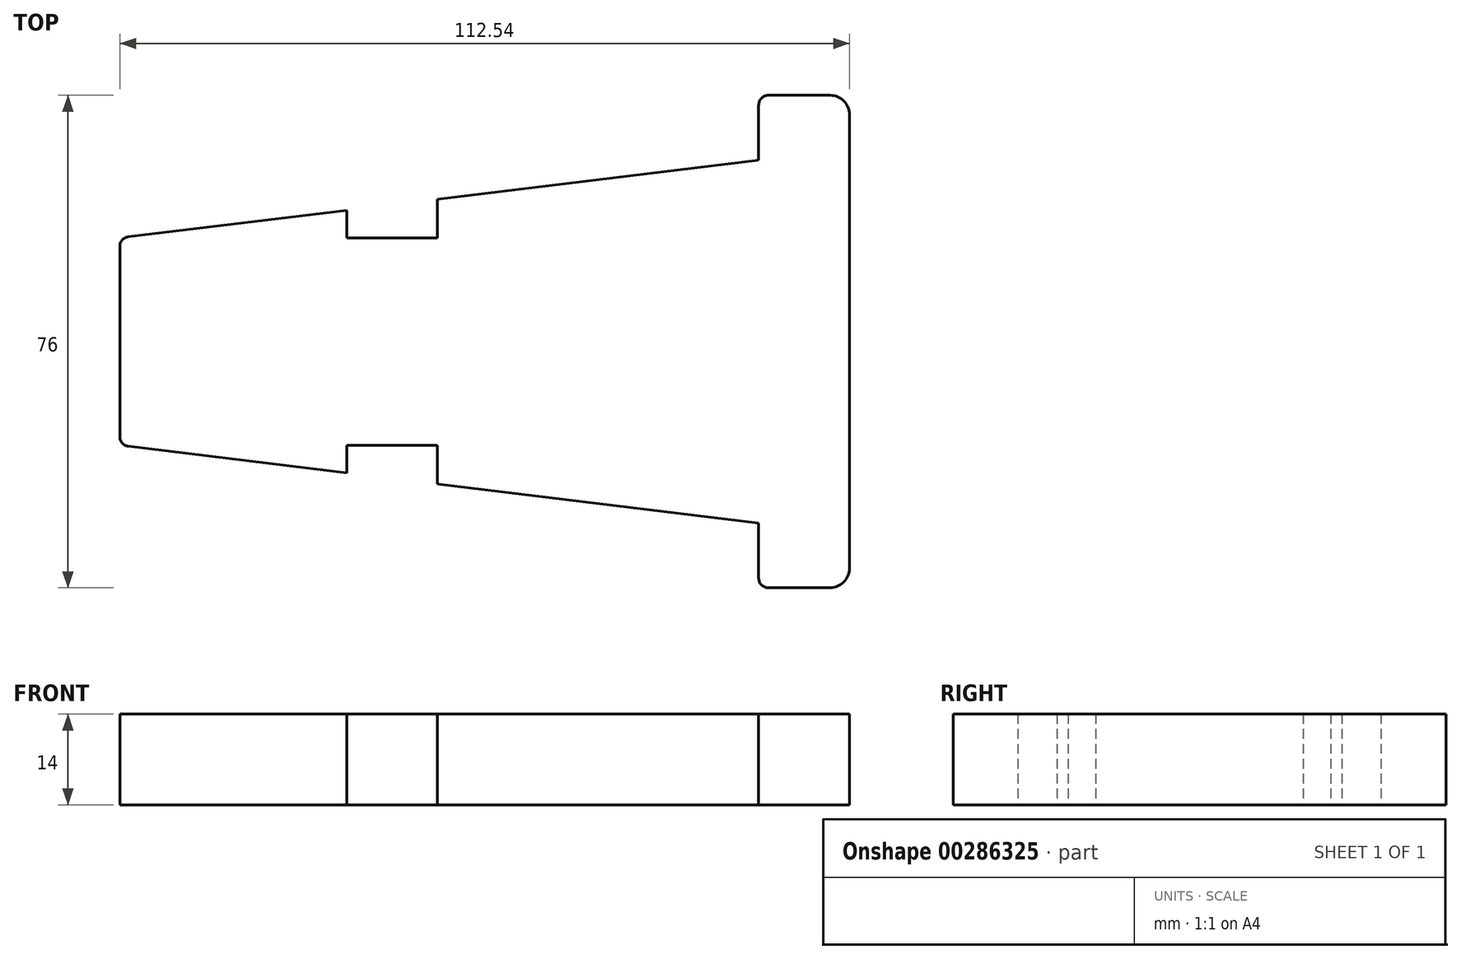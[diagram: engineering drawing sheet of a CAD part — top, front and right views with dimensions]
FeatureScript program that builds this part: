
annotation { "Feature Type Name" : "Feature", "Feature Type Description" : "" }
export const myFeature = defineFeature(function(context is Context, id is Id, definition is map)
    precondition{}
    {
        {
            var Q0;
            Q0=qCreatedBy(makeId("Top.planeOp"),FACE);
            var sketch = newSketch(context, id + "F0", { "sketchPlane" : qUnion([Q0])});
            skLineSegment(sketch, "E0", {"start": v(56.71, 35) * mm, "end": v(56.71, -35) * mm});
            skLineSegment(sketch, "E1", {"start": v(53.71, 38) * mm, "end": v(44.21, 38) * mm});
            skLineSegment(sketch, "E2", {"start": v(53.71, -38) * mm, "end": v(44.21, -38) * mm});
            skLineSegment(sketch, "E3", {"start": v(42.71, 36.5) * mm, "end": v(42.71, 28) * mm});
            skLineSegment(sketch, "E4", {"start": v(42.71, -36.5) * mm, "end": v(42.71, -28) * mm});
            skPoint(sketch, "E5.orphan", {"position": v(21.88, 18) * mm});
            skPoint(sketch, "E6.orphan", {"position": v(21.88, -18) * mm});
            skPoint(sketch, "E7.visualSharp", {"position": v(56.71, 38) * mm});
            skArc(sketch, "E7.filletArc", {"start": v(56.71, 35) * mm, "mid": v(55.83, 37.12) * mm, "end": v(53.71, 38) * mm});
            skPoint(sketch, "E8.visualSharp", {"position": v(56.71, -38) * mm});
            skArc(sketch, "E8.filletArc", {"start": v(53.71, -38) * mm, "mid": v(55.83, -37.12) * mm, "end": v(56.71, -35) * mm});
            skPoint(sketch, "E9.visualSharp", {"position": v(-41.66, 14) * mm});
            skPoint(sketch, "E10.visualSharp", {"position": v(-48.29, -18) * mm});
            skPoint(sketch, "E11.visualSharp", {"position": v(42.71, 38) * mm});
            skArc(sketch, "E11.filletArc", {"start": v(44.21, 38) * mm, "mid": v(43.15, 37.56) * mm, "end": v(42.71, 36.5) * mm});
            skPoint(sketch, "E12.start.orphan", {"position": v(6.97, 15.5) * mm});
            skPoint(sketch, "E13.start.orphan", {"position": v(6.97, -18) * mm});
            skPoint(sketch, "E14.start.orphan", {"position": v(-6.83, -18) * mm});
            skLineSegment(sketch, "E15", {"start": v(6.97, 15.5) * mm, "end": v(6.97, 14) * mm});
            skLineSegment(sketch, "E16.trimOffspring", {"start": v(-6.86, 14) * mm, "end": v(-6.83, 14) * mm});
            skLineSegment(sketch, "E17", {"start": v(6.97, -18) * mm, "end": v(6.97, -17.77) * mm});
            skLineSegment(sketch, "E18.trimOffspring", {"start": v(-6.85, -17.83) * mm, "end": v(-6.83, -17.83) * mm});
            skPoint(sketch, "E19.visualSharp", {"position": v(42.71, -38) * mm});
            skArc(sketch, "E19.filletArc", {"start": v(42.71, -36.5) * mm, "mid": v(43.15, -37.56) * mm, "end": v(44.21, -38) * mm});
            skLineSegment(sketch, "E20", {"start": v(-6.83, -17.83) * mm, "end": v(-6.83, -18) * mm});
            skLineSegment(sketch, "E21", {"start": v(-55.83, 0) * mm, "end": v(-55.83, -16) * mm});
            skLineSegment(sketch, "E22", {"start": v(-55.83, -14.67) * mm, "end": v(-55.83, 0) * mm});
            skLineSegment(sketch, "E23", {"start": v(-55.83, 14.67) * mm, "end": v(-55.83, 0) * mm});
            skLineSegment(sketch, "E24", {"start": v(-54.52, -16.16) * mm, "end": v(-20.83, -20.26) * mm});
            skLineSegment(sketch, "E25", {"start": v(-54.52, 16.16) * mm, "end": v(-20.83, 20.26) * mm});
            skLineSegment(sketch, "E26", {"start": v(-20.83, 16) * mm, "end": v(-6.83, 16) * mm});
            skLineSegment(sketch, "E27", {"start": v(-20.83, -16) * mm, "end": v(-6.83, -16) * mm});
            skLineSegment(sketch, "E28", {"start": v(-6.83, -16) * mm, "end": v(-6.83, -21.97) * mm});
            skLineSegment(sketch, "E29", {"start": v(-6.83, 16) * mm, "end": v(-6.83, 21.97) * mm});
            skLineSegment(sketch, "E30", {"start": v(-20.83, -20.26) * mm, "end": v(-20.83, -16) * mm});
            skLineSegment(sketch, "E31", {"start": v(-20.83, 16) * mm, "end": v(-20.83, 20.26) * mm});
            skLineSegment(sketch, "E32.trimOffspring", {"start": v(-6.83, 21.97) * mm, "end": v(42.71, 28) * mm});
            skLineSegment(sketch, "E33.trimOffspring", {"start": v(-6.83, -21.97) * mm, "end": v(42.71, -28) * mm});
            skPoint(sketch, "E34.visualSharp", {"position": v(-55.83, 16) * mm});
            skArc(sketch, "E34.filletArc", {"start": v(-54.52, 16.16) * mm, "mid": v(-55.46, 15.67) * mm, "end": v(-55.83, 14.67) * mm});
            skPoint(sketch, "E35.visualSharp", {"position": v(-55.83, -16) * mm});
            skArc(sketch, "E35.filletArc", {"start": v(-55.83, -14.67) * mm, "mid": v(-55.46, -15.67) * mm, "end": v(-54.52, -16.16) * mm});
            skSolve(sketch);
        }
        {
            var Q0;
            Q0=makeQuery(id+"F0.imprint","IMPRINT",FACE,{"disambiguationData":[TD([[makeQuery(id+"F0.imprint","IMPRINT",EDGE,{"derivedFrom":sQuery(id+"F0.wireOp",EDGE,"E0")}),-1.0]])]});
            extrude(context, id + "F1", {"entities" : qUnion([Q0]), "depth" : 14 * mm});
        }
    });
